FCSTD DOCUMENT  (FreeCAD 0.16R6707 (Git))
Label: Areas Planes 
License: All rights reserved
LicenseURL: http://en.wikipedia.org/wiki/All_rights_reserved
objects: App::FeaturePython×6, Part::Part2DObjectPython×3, App::DocumentObjectGroup×3
note: 3 computed .brp shape members not serialized (recipe doc carries the construction recipe); baked Part::Feature solids carry a one-line shape summary decoded from their .brp

FEATURE [Part::Part2DObjectPython] Rectangle  # Draft 2D object (typed FeaturePython)
  ChamferSize = 0
  Columns = 1
  FilletRadius = 0
  Height = 7500
  Length = 6000
  MakeFace = true
  MapMode = -1
  Placement = pos=(-92,-160,0) rot=(0,0,1;0rad)
  Rows = 1
FEATURE [App::FeaturePython] Dimension  # Draft dimension (typed FeaturePython)
  Diameter = false
  Dimline = (6612,4842,0)
  Direction = (0,0,0)
  Distance = 7500
  End = (5908,7340,0)
  LinkedGeometry = -> [Rectangle]
  Normal = (0,0,1)
  Start = (5908,-160,0)
  Support = -> Rectangle
FEATURE [App::FeaturePython] Dimension001  # Draft dimension (typed FeaturePython)
  Diameter = false
  Dimline = (3172,-852,0)
  Direction = (0,0,0)
  Distance = 6000
  End = (5908,-160,0)
  LinkedGeometry = -> [Rectangle]
  Normal = (0,0,1)
  Start = (-92,-160,0)
  Support = -> Rectangle
FEATURE [App::DocumentObjectGroup] Group  label="7.5mx6m"
  Group = -> [Dimension,Dimension001,Rectangle]
FEATURE [Part::Part2DObjectPython] Rectangle001  # Draft 2D object (typed FeaturePython)
  ChamferSize = 0
  Columns = 1
  FilletRadius = 0
  Height = 9000
  Length = 5000
  MakeFace = true
  MapMode = -1
  Placement = pos=(9194.87,-160,0) rot=(0,0,1;0rad)
  Rows = 1
FEATURE [App::FeaturePython] Dimension002  # Draft dimension (typed FeaturePython)
  Diameter = false
  Dimline = (15053,4856,0)
  Direction = (0,0,0)
  Distance = 9000
  End = (14194.9,8840,0)
  LinkedGeometry = -> [Rectangle001]
  Normal = (0,0,1)
  Start = (14194.9,-160,0)
  Support = -> Rectangle001
FEATURE [App::FeaturePython] Dimension003  # Draft dimension (typed FeaturePython)
  Diameter = false
  Dimline = (12458.9,-852,0)
  Direction = (0,0,0)
  Distance = 5000
  End = (14194.9,-160,0)
  LinkedGeometry = -> [Rectangle001]
  Normal = (0,0,1)
  Start = (9194.87,-160,0)
  Support = -> Rectangle001
FEATURE [App::DocumentObjectGroup] Group001  label="9mx5m"
  Group = -> [Dimension002,Dimension003,Rectangle001]
FEATURE [Part::Part2DObjectPython] Rectangle002  # Draft 2D object (typed FeaturePython)
  ChamferSize = 0
  Columns = 1
  FilletRadius = 0
  Height = 11250
  Length = 4000
  MakeFace = true
  MapMode = -1
  Placement = pos=(17670.3,-160,0) rot=(0,0,1;0rad)
  Rows = 1
FEATURE [App::FeaturePython] Dimension004  # Draft dimension (typed FeaturePython)
  Diameter = false
  Dimline = (22786,4857,0)
  Direction = (0,0,0)
  Distance = 11250
  End = (21670.3,11090,0)
  LinkedGeometry = -> [Rectangle002]
  Normal = (0,0,1)
  Start = (21670.3,-160,0)
  Support = -> Rectangle002
FEATURE [App::FeaturePython] Dimension005  # Draft dimension (typed FeaturePython)
  Diameter = false
  Dimline = (20934.3,-852,0)
  Direction = (0,0,0)
  Distance = 4000
  End = (21670.3,-160,0)
  LinkedGeometry = -> [Rectangle002]
  Normal = (0,0,1)
  Start = (17670.3,-160,0)
  Support = -> Rectangle002
FEATURE [App::DocumentObjectGroup] Group002  label="11.5mx4m"
  Group = -> [Dimension004,Dimension005,Rectangle002]
